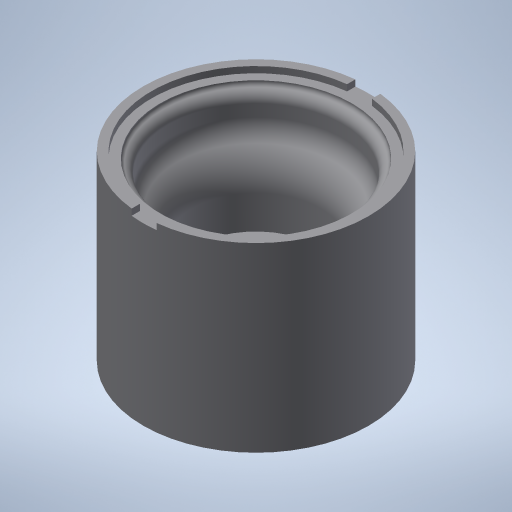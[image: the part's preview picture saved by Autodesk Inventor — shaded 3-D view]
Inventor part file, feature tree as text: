
AUTODESK INVENTOR PART (.ipt)
format: ipt  version: 2023.3 (Build 273359000, 359)  size: 1,011,712 bytes
history: native  units: mm
features: other x6, sketch x5, boolean_combine x2, hole x2, extrude x2, chamfer x2, revolve x1, emboss x1, mirror x1, draft x1
ambient origin geometry x8: Origin, YZ Plane, XZ Plane, XY Plane, X Axis, Y Axis, Z Axis, Center Point
bodies: Solid3 (feature_tree), Solid1 (feature_tree)
feature tree (23):
  other  "Mold_1_Sealing_ring_20x1_silicone_x.ipt"
  other  "Sealing_ring_20x1_silicone_h.ipt"
  revolve  "Revolution1"  [1 undecoded]
  boolean_combine  "Combine1"
  boolean_combine  "Combine2"
  hole  "Hole1"  [1 undecoded]
  extrude  "Extrusion1"  Depth=10.0mm TaperAngle=0.0deg
  hole  "Hole2"  [1 undecoded]
  extrude  "Extrusion2"  Depth=1.5mm
  chamfer  "Chamfer2"  Distance=0.1mm
  emboss  "Emboss1"
  mirror  "Mirror1"
  draft  "FaceDraft1"
  chamfer  "Chamfer1"  Distance=15.0mm
  other  "Solid1::Mold_1_Sealing_ring_20x1_silicone_x.ipt"
  other  "TaggingFeature1"
  other  "Solid1::Sealing_ring_20x1_silicone_h.ipt"
  other  "TaggingFeature2"
  sketch  "Sketch1"  dims[d0=10.0mm d1=10.0mm]
  sketch  "Sketch3"  dims[d3=360.0deg]
  sketch  "Sketch4"  dims[d4=10.5mm d5=6.0mm d6=12.6mm d7=2.0mm d8=90.0deg d9=8.0mm d10=20.594885mm d11=0.5mm d12=2.0mm d13=45.0deg]
  sketch  "Sketch5"  dims[d14=1.5mm d17=10.0mm d18=0.0mm]
  sketch  "Sketch6"  dims[d19=6.0mm d20=0.55mm d21=1.5mm d22=6.0mm d23=4.0mm d24=2.0mm d25=90.0deg d26=20.5mm d27=0.0mm d30=0.1mm d31=15.0mm d32=2.0mm d33=1.5mm d34=17.1mm d35=9.0mm d36=0.0mm d37=1.0mm d38=1.0mm d39=0.05mm d40=0.5mm d41=2.5mm d42=0.1mm d43=-0.872665mm d44=15.0mm d45=2.0mm d46=1.745329mm d47=0.2mm d48=0.0mm]
note: 3 required parameter values undecoded (feature->parameter linkage not recoverable at this tier; creation-order binding heuristic only, values carry confidence <= 0.55)